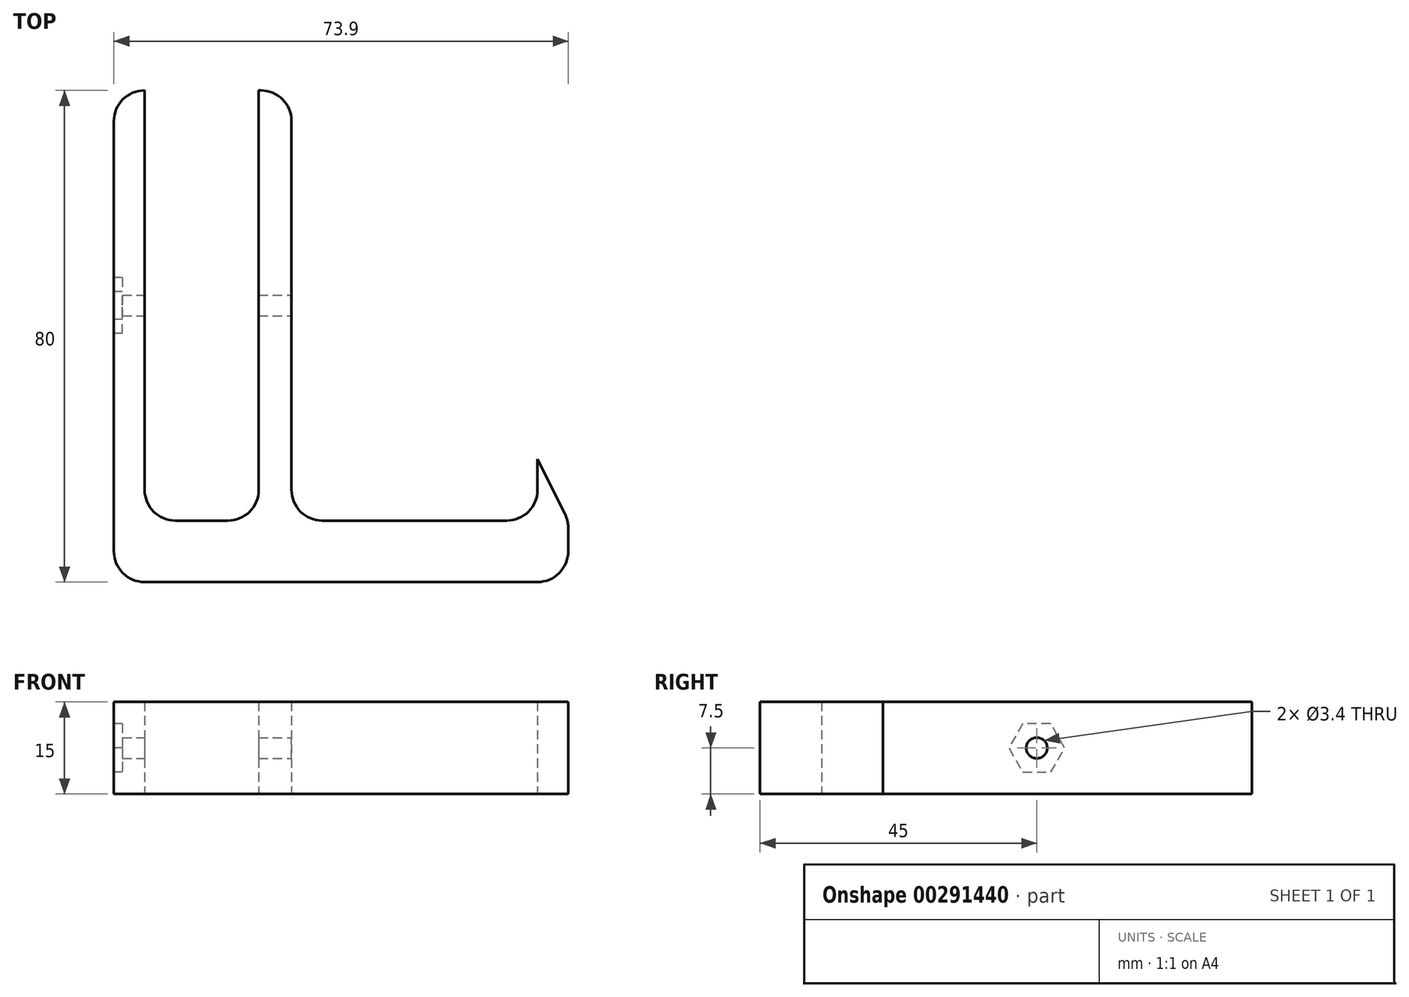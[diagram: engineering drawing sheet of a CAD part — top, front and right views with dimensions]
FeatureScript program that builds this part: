
annotation { "Feature Type Name" : "Feature", "Feature Type Description" : "" }
export const myFeature = defineFeature(function(context is Context, id is Id, definition is map)
    precondition{}
    {
        {
            var Q0;
            Q0=qCreatedBy(makeId("Top.planeOp"),FACE);
            var sketch = newSketch(context, id + "F0", { "sketchPlane" : qUnion([Q0])});
            skLineSegment(sketch, "E0.bottom", {"start": v(9.28, -35) * mm, "end": v(-9.27, -35) * mm});
            skLineSegment(sketch, "E0.left", {"start": v(9.28, -35) * mm, "end": v(9.28, 35) * mm});
            skLineSegment(sketch, "E0.right", {"start": v(-9.27, -35) * mm, "end": v(-9.27, 35) * mm});
            skPoint(sketch, "E0.middle", {"position": v(0, 0) * mm});
            skLineSegment(sketch, "E1", {"start": v(9.28, 35) * mm, "end": v(14.62, 35) * mm});
            skLineSegment(sketch, "E2", {"start": v(14.62, 35) * mm, "end": v(14.62, -35) * mm});
            skLineSegment(sketch, "E3", {"start": v(14.62, -35) * mm, "end": v(54.62, -35) * mm});
            skLineSegment(sketch, "E4", {"start": v(54.62, -35) * mm, "end": v(54.62, -25) * mm});
            skLineSegment(sketch, "E5", {"start": v(54.62, -35) * mm, "end": v(59.62, -35) * mm, "construction": true});
            skLineSegment(sketch, "E6", {"start": v(54.62, -25) * mm, "end": v(59.62, -35) * mm});
            skLineSegment(sketch, "E7", {"start": v(59.62, -35) * mm, "end": v(59.62, -45) * mm});
            skLineSegment(sketch, "E8", {"start": v(-9.27, 35) * mm, "end": v(-14.28, 35) * mm});
            skLineSegment(sketch, "E9", {"start": v(-14.28, 35) * mm, "end": v(-14.28, -35) * mm});
            skLineSegment(sketch, "E10", {"start": v(59.62, -45) * mm, "end": v(-14.27, -45) * mm});
            skLineSegment(sketch, "E11", {"start": v(-14.28, -45) * mm, "end": v(-14.28, -35) * mm});
            skSolve(sketch);
        }
        {
            var Q0;
            Q0 = qSketchRegion(id + "F0", true);
            extrude(context, id + "F1", {"entities" : qUnion([Q0]), "depth" : 15 * mm});
        }
        {
            var Q0;
            Q0=makeQuery(id+"F1.opExtrude","SWEPT_FACE",FACE,{"disambiguationData":[OSD([sQuery(id+"F0.wireOp",EDGE,"E2")])]});
            var sketch = newSketch(context, id + "F2", { "sketchPlane" : qUnion([Q0])});
            skLineSegment(sketch, "E12", {"start": v(0, 7.5) * mm, "end": v(35, 7.5) * mm, "construction": true});
            skPoint(sketch, "E12.endSnap0", {"position": v(0, 15) * mm});
            skCircle(sketch, "E13", {"center": v(0, 7.5) * mm, "radius": 1.7 * mm});
            skSolve(sketch);
        }
        {
            var Q0;
            Q0 = qSketchRegion(id + "F2", true);
            extrude(context, id + "F3", {"entities" : qUnion([Q0]), "operationType" : NewBodyOperationType.REMOVE, "endBound" : BoundingType.THROUGH_ALL, "oppositeDirection" : true, "depth" : 25 * mm});
        }
        {
            var Q0;
            Q0=makeQuery(id+"F1.opExtrude","SWEPT_FACE",FACE,{"disambiguationData":[OSD([sQuery(id+"F0.wireOp",EDGE,"E9"),sQuery(id+"F0.wireOp",EDGE,"E11")])]});
            var sketch = newSketch(context, id + "F4", { "sketchPlane" : qUnion([Q0])});
            skLineSegment(sketch, "E14", {"start": v(-35, 7.5) * mm, "end": v(0, 7.5) * mm, "construction": true});
            skCircle(sketch, "E15.cCircle", {"center": v(0, 7.5) * mm, "radius": 3.93 * mm, "construction": true});
            skLineSegment(sketch, "E15.0", {"start": v(2.27, 3.57) * mm, "end": v(-2.27, 3.57) * mm});
            skLineSegment(sketch, "E15.1", {"start": v(-2.27, 3.57) * mm, "end": v(-4.54, 7.5) * mm});
            skLineSegment(sketch, "E15.2", {"start": v(-4.54, 7.5) * mm, "end": v(-2.27, 11.43) * mm});
            skLineSegment(sketch, "E15.3", {"start": v(-2.27, 11.43) * mm, "end": v(2.27, 11.43) * mm});
            skLineSegment(sketch, "E15.4", {"start": v(2.27, 11.43) * mm, "end": v(4.54, 7.5) * mm});
            skLineSegment(sketch, "E15.5", {"start": v(4.54, 7.5) * mm, "end": v(2.27, 3.57) * mm});
            skPoint(sketch, "E15.0.midPoint", {"position": v(0, 3.57) * mm});
            skSolve(sketch);
        }
        {
            var Q0;
            Q0 = qSketchRegion(id + "F4", true);
            extrude(context, id + "F5", {"entities" : qUnion([Q0]), "operationType" : NewBodyOperationType.REMOVE, "oppositeDirection" : true, "depth" : 1.38 * mm});
        }
        {
            var Q0;
            Q0=makeQuery(id+"F1.opExtrude","SWEPT_EDGE",EDGE,{"disambiguationData":[OSD([sQuery(id+"F0.wireOp",EDGE,"E0.bottom"),sQuery(id+"F0.wireOp",EDGE,"E0.right")])]});
            var Q1;
            Q1=makeQuery(id+"F1.opExtrude","SWEPT_EDGE",EDGE,{"disambiguationData":[OSD([sQuery(id+"F0.wireOp",EDGE,"E0.bottom"),sQuery(id+"F0.wireOp",EDGE,"E0.left")])]});
            var Q2;
            Q2=makeQuery(id+"F1.opExtrude","SWEPT_EDGE",EDGE,{"disambiguationData":[OSD([sQuery(id+"F0.wireOp",EDGE,"E10"),sQuery(id+"F0.wireOp",EDGE,"E11")])]});
            var Q3;
            Q3=makeQuery(id+"F1.opExtrude","SWEPT_EDGE",EDGE,{"disambiguationData":[OSD([sQuery(id+"F0.wireOp",EDGE,"E7"),sQuery(id+"F0.wireOp",EDGE,"E10")])]});
            var Q4;
            Q4=makeQuery(id+"F1.opExtrude","SWEPT_EDGE",EDGE,{"disambiguationData":[OSD([sQuery(id+"F0.wireOp",EDGE,"E3"),sQuery(id+"F0.wireOp",EDGE,"E4")])]});
            var Q5;
            Q5=makeQuery(id+"F1.opExtrude","SWEPT_EDGE",EDGE,{"disambiguationData":[OSD([sQuery(id+"F0.wireOp",EDGE,"E2"),sQuery(id+"F0.wireOp",EDGE,"E3")])]});
            var Q6;
            Q6=makeQuery(id+"F1.opExtrude","SWEPT_EDGE",EDGE,{"disambiguationData":[OSD([sQuery(id+"F0.wireOp",EDGE,"E6"),sQuery(id+"F0.wireOp",EDGE,"E7")])]});
            var Q7;
            Q7=makeQuery(id+"F1.opExtrude","SWEPT_EDGE",EDGE,{"disambiguationData":[OSD([sQuery(id+"F0.wireOp",EDGE,"E1"),sQuery(id+"F0.wireOp",EDGE,"E2")])]});
            var Q8;
            Q8=makeQuery(id+"F1.opExtrude","SWEPT_EDGE",EDGE,{"disambiguationData":[OSD([sQuery(id+"F0.wireOp",EDGE,"E8"),sQuery(id+"F0.wireOp",EDGE,"E9")])]});
            fillet(context, id + "F6", {"entities" : qUnion([Q0, Q1, Q2, Q3, Q4, Q5, Q6, Q7, Q8]), "radius" : 5 * mm, "tangentPropagation" : true, "allowEdgeOverflow" : false});
        }
    });
